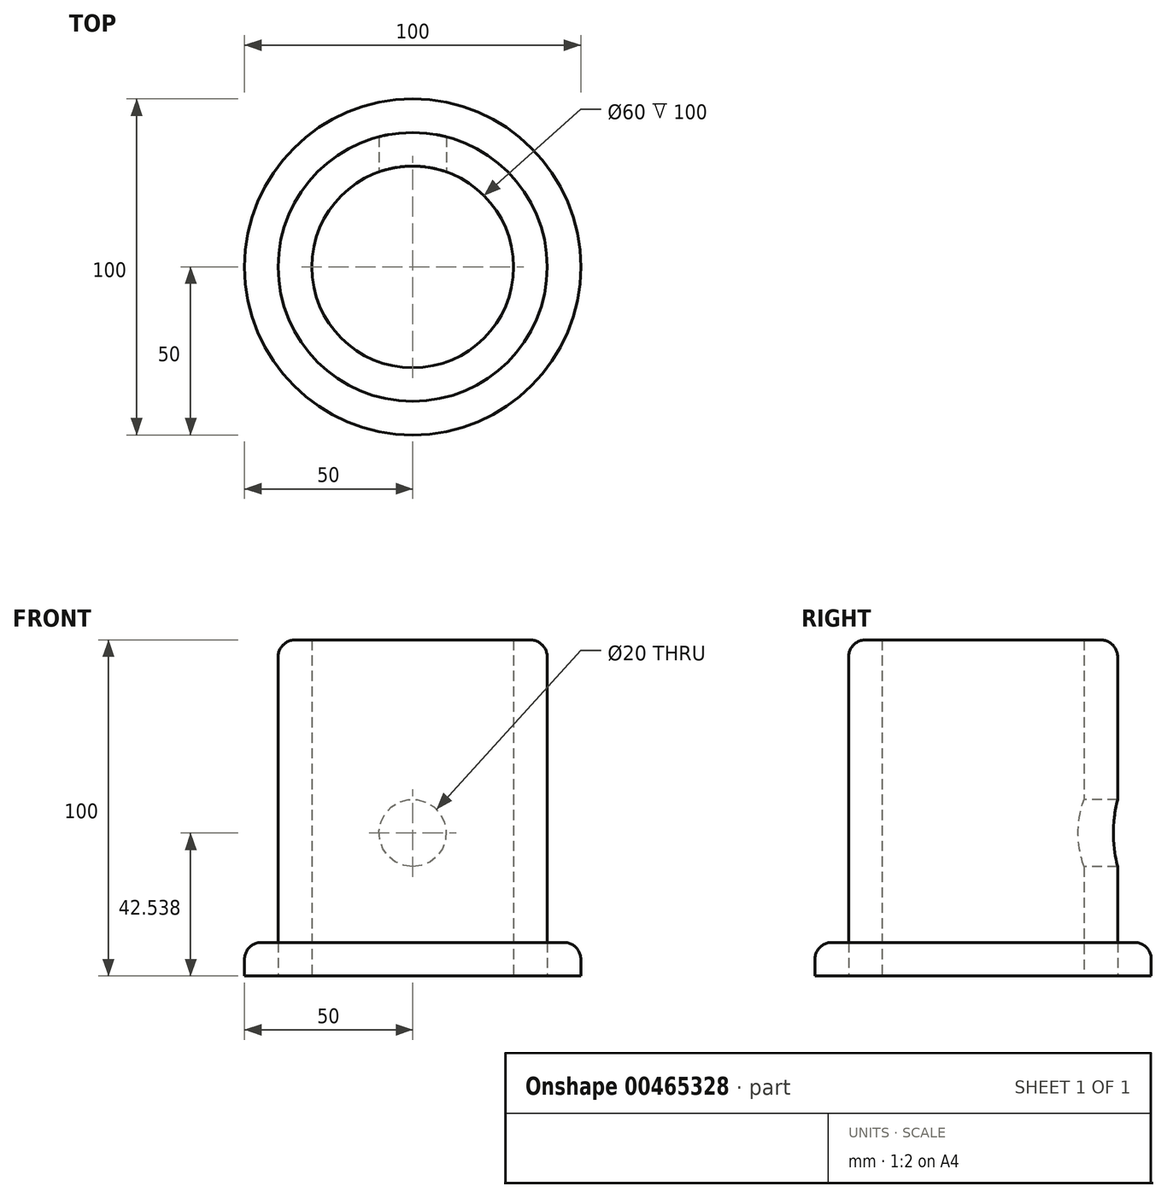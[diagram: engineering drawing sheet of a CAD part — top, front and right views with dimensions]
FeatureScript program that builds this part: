
annotation { "Feature Type Name" : "Feature", "Feature Type Description" : "" }
export const myFeature = defineFeature(function(context is Context, id is Id, definition is map)
    precondition{}
    {
        {
            var Q0;
            Q0=qCreatedBy(makeId("Top.planeOp"),FACE);
            var sketch = newSketch(context, id + "F0", { "sketchPlane" : qUnion([Q0])});
            skCircle(sketch, "E0", {"center": v(0, 0) * mm, "radius": 50 * mm});
            skSolve(sketch);
        }
        {
            var Q0;
            Q0=makeQuery(id+"F0.imprint","IMPRINT",FACE,{"disambiguationData":[TD([[makeQuery(id+"F0.imprint","IMPRINT",EDGE,{"derivedFrom":sQuery(id+"F0.wireOp",EDGE,"E0")}),1.0]])]});
            extrude(context, id + "F1", {"entities" : qUnion([Q0]), "depth" : 10 * mm});
        }
        {
            var Q0;
            Q0=qCreatedBy(makeId("Top.planeOp"),FACE);
            var sketch = newSketch(context, id + "F2", { "sketchPlane" : qUnion([Q0])});
            skCircle(sketch, "E1", {"center": v(0, 0) * mm, "radius": 40 * mm});
            skCircle(sketch, "E2.0", {"center": v(0, 0) * mm, "radius": 30 * mm});
            skSolve(sketch);
        }
        {
            var Q0;
            Q0=makeQuery(id+"F2.imprint","IMPRINT",FACE,{"disambiguationData":[TD([[makeQuery(id+"F2.imprint","IMPRINT",EDGE,{"derivedFrom":sQuery(id+"F2.wireOp",EDGE,"E1")}),1.0]])]});
            extrude(context, id + "F3", {"entities" : qUnion([Q0]), "depth" : 100 * mm});
        }
        {
            var Q0;
            Q0=makeQuery(id+"F3.opExtrude","CAP_EDGE",EDGE,{"disambiguationData":[OSD([sQuery(id+"F2.wireOp",EDGE,"E1")])],"isStart":false});
            var Q1;
            Q1=makeQuery(id+"F1.opExtrude","CAP_EDGE",EDGE,{"disambiguationData":[OSD([sQuery(id+"F0.wireOp",EDGE,"E0")])],"isStart":false});
            fillet(context, id + "F4", {"entities" : qUnion([Q0, Q1]), "radius" : 5 * mm, "tangentPropagation" : true, "allowEdgeOverflow" : false});
        }
        {
            var Q0;
            Q0=qCreatedBy(makeId("Front.planeOp"),FACE);
            var sketch = newSketch(context, id + "F5", { "sketchPlane" : qUnion([Q0])});
            skPoint(sketch, "E3", {"position": v(0, 42.54) * mm});
            skSolve(sketch);
        }
        {
            var Q0;
            Q0=sQuery(id+"F5.wireOp",VERTEX,"E3");
            var Q1;
            Q1=makeQuery(id+"F3.opExtrude","SWEPT_BODY",BODY,{"disambiguationData":[OSD([sQuery(id+"F2.wireOp",EDGE,"E1"),sQuery(id+"F2.wireOp",EDGE,"E2.0")])]});
            hole(context, id + "F6", {"style" : HoleStyle.SIMPLE, "endStyle" : HoleEndStyle.THROUGH, "holeDiameter" : 20 * mm, "isTappedThrough" : true, "tappedDepth" : 12 * mm, "tapClearance" : 3, "locations" : qUnion([Q0]), "scope" : qUnion([Q1])});
        }
    });
